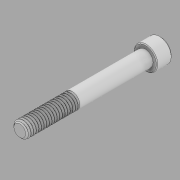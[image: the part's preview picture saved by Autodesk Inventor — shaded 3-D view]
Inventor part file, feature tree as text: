
AUTODESK INVENTOR PART (.ipt)
format: ipt  version: 2020 (Build 240168000, 168)  size: 536,064 bytes
history: native  units: in
note: dims shown in document units (in); Inventor stores cm internally (conversion verified against a paired STEP export)
features: chamfer x1
ambient origin geometry x8: Origin, YZ Plane, XZ Plane, XY Plane, X Axis, Y Axis, Z Axis, Center Point
bodies: Solid1 (feature_tree)
feature tree (1):
  chamfer  "Chamfer2"  [1 undecoded]
note: 1 required parameter value undecoded (feature->parameter linkage not recoverable at this tier; creation-order binding heuristic only, values carry confidence <= 0.55)
